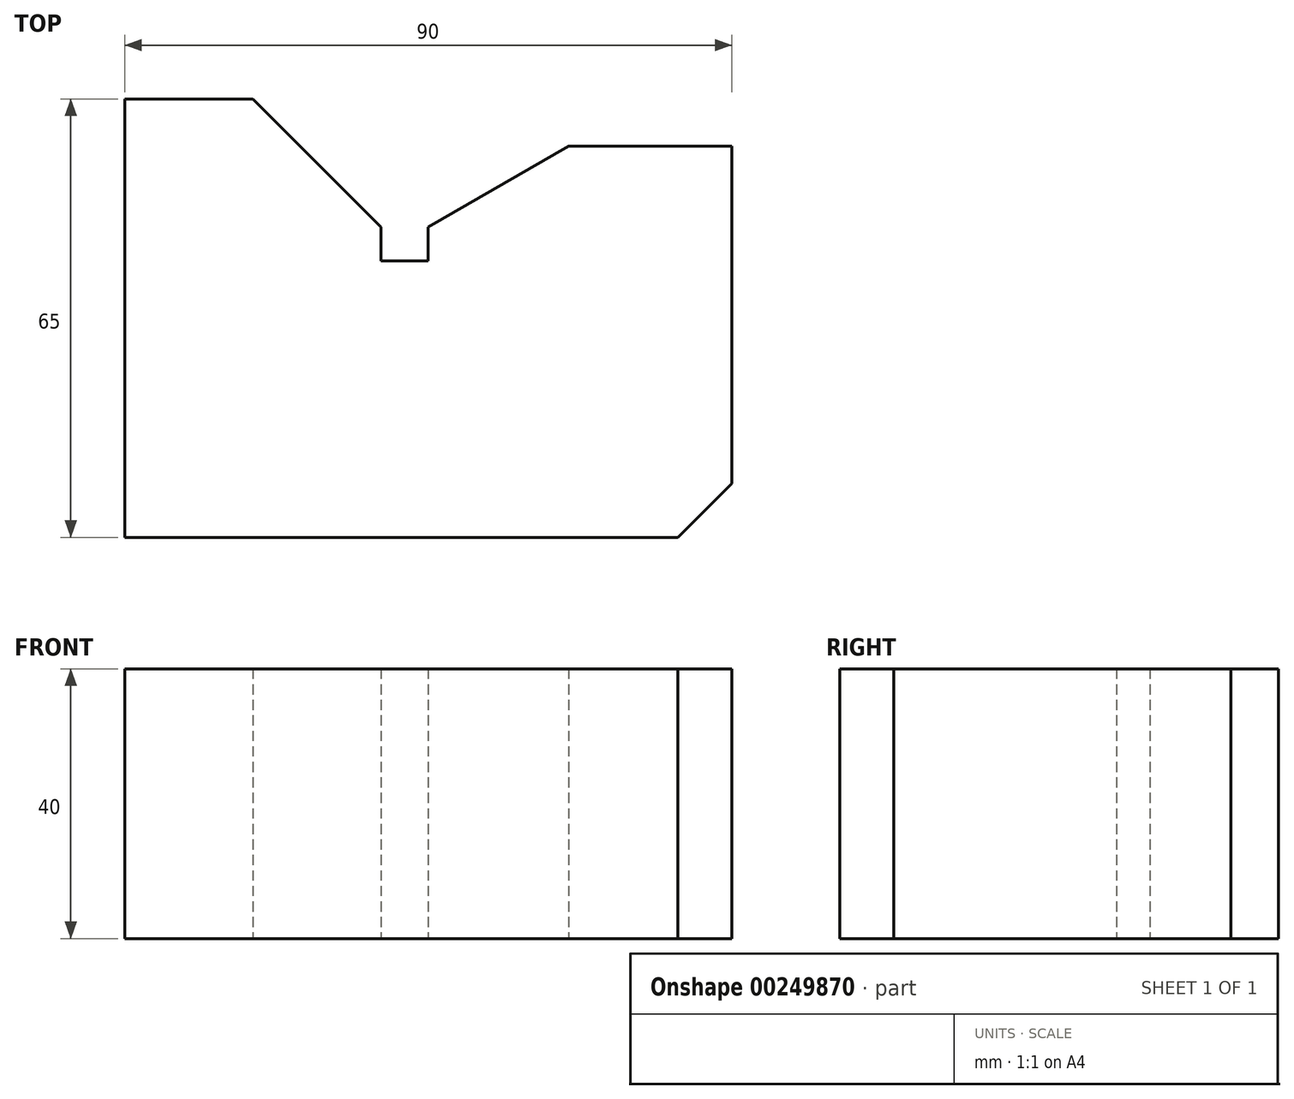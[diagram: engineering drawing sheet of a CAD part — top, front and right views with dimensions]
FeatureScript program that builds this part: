
annotation { "Feature Type Name" : "Feature", "Feature Type Description" : "" }
export const myFeature = defineFeature(function(context is Context, id is Id, definition is map)
    precondition{}
    {
        {
            var Q0;
            Q0=qCreatedBy(makeId("Top.planeOp"),FACE);
            var sketch = newSketch(context, id + "F0", { "sketchPlane" : qUnion([Q0])});
            skLineSegment(sketch, "E0", {"start": v(-41.18, 50.38) * mm, "end": v(-41.18, -14.62) * mm});
            skLineSegment(sketch, "E1", {"start": v(-41.18, -14.62) * mm, "end": v(40.82, -14.62) * mm});
            skLineSegment(sketch, "E2", {"start": v(40.82, -14.62) * mm, "end": v(48.82, -6.62) * mm});
            skLineSegment(sketch, "E3", {"start": v(48.82, -6.62) * mm, "end": v(48.82, 43.38) * mm});
            skLineSegment(sketch, "E4", {"start": v(48.82, 43.38) * mm, "end": v(24.6, 43.38) * mm});
            skLineSegment(sketch, "E5", {"start": v(24.6, 43.38) * mm, "end": v(3.82, 31.38) * mm});
            skLineSegment(sketch, "E6", {"start": v(3.82, 31.38) * mm, "end": v(3.82, 26.38) * mm});
            skLineSegment(sketch, "E7", {"start": v(3.82, 26.38) * mm, "end": v(-3.18, 26.38) * mm});
            skLineSegment(sketch, "E8", {"start": v(-3.18, 26.38) * mm, "end": v(-3.18, 31.38) * mm});
            skLineSegment(sketch, "E9", {"start": v(-3.18, 31.38) * mm, "end": v(-22.18, 50.38) * mm});
            skLineSegment(sketch, "E10", {"start": v(-22.18, 50.38) * mm, "end": v(-41.18, 50.38) * mm});
            skSolve(sketch);
        }
        {
            var Q0;
            Q0=makeQuery(id+"F0.imprint","IMPRINT",FACE,{"disambiguationData":[TD([[makeQuery(id+"F0.imprint","IMPRINT",EDGE,{"derivedFrom":sQuery(id+"F0.wireOp",EDGE,"E0")}),1.0]])]});
            extrude(context, id + "F1", {"entities" : qUnion([Q0]), "depth" : 40 * mm});
        }
    });
